# Revit family: SLS CM
name_source: partatom
category: Lighting Fixtures
revit_build: Autodesk Revit 2013 (Build: 20130531_2115(x64)
units: mm (PartAtom-declared; Revit-internal decimal feet)

## types (5) — shared parameters
Color Filter = 16777215
Default Elevation = 4' - 0"
Description = Solaris utilizes modern small-ballast technology for a compact, contemporary look.
Dimming Lamp Color Temperature Shift = <None>
Emit Shape Visible in Rendering = No
Emit from Rectangle Length = 3' - 10"
Emit from Rectangle Width = 0' - 7"
Glass = Hubbell - White Glass
Housing Material = Hubbell - White
Lamp = T5, T5HO, T8
Load Classification = Lighting
Manufacturer = Alera Lighting
Model = SLS-CM
Power Factor = 1
Product Documentation Link = https://hubbellcdn.com
Product Page URL = https://www.hubbell.com
Row Length = 4' - 0"
Suspension Height = 4' - 0"
Tilt Angle = 90.00°
URL = https://www.hubbell.com
Voltage = 120 V

## per-type parameters (varying)
| type | Apparent Load | Assembly Code | Distribution | Lamp Type | Photometric Web File | Watts |
| SLS-1T80/100-SP-E | 34 VA |  | 0% Uplight, 100% Downlight | One T8 Lamp | SLS-1T80 100-SP-E.ies | 34 W |
| SLS-3T885/15-SP-E | 87 VA | D5020200 | 85% Uplight, 15% Downlight | Three T8 Lamps | SLS-3T885 15-SP-E.ies | 87 W |
| SLS-3T8-LD-E | 89 VA |  | 60% Uplight, 40% Downlight | Three T8 Lamps | SLS-3T8-LD-E.ies | 89 W |
| SLS-2T8-A12-E | 58 VA |  | 60% Uplight, 40% Downlight | Two T8 Lamps | SLS-2T8-A12-E.ies | 58 W |
| SLS-1T5HO0/100-LD-EP | 53 VA |  | 0% Uplight, 100% Downlight | One T5 Lamp | SLS-1T5HO0 100-LD-EP.ies | 53 W |

## geometry (parser evidence)
native form markers: Blend x4, Sweep x4
no freeform markers — native parametric forms only
